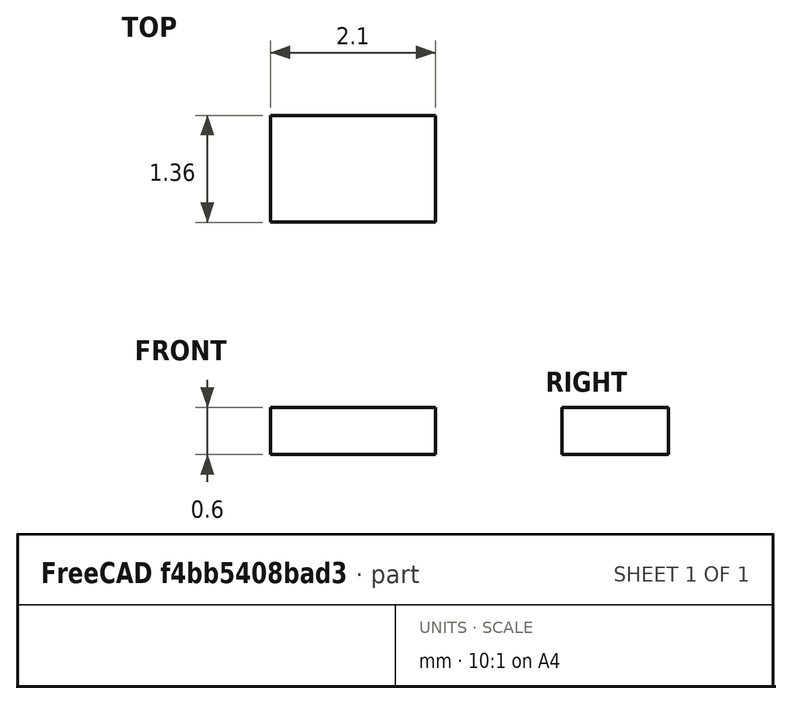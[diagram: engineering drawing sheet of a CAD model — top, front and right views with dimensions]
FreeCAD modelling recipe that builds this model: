
FCSTD DOCUMENT  (FreeCAD 0.18R15969 (Git))
Label: Resistor 10k
License: All rights reserved
LicenseURL: http://en.wikipedia.org/wiki/All_rights_reserved
objects: Sketcher::SketchObject×1, PartDesign::Pad×1, PartDesign::Body×1
note: 4 computed .brp shape members not serialized (recipe doc carries the construction recipe); baked Part::Feature solids carry a one-line shape summary decoded from their .brp

FEATURE [Sketcher::SketchObject] Sketch
  MapMode = 5
  Support = -> [XY_Plane]
  expr: Constraints[16] = 2 + 0.1
  expr: Constraints[17] = 1.25 + 0.1
  sketch-geometry (7):
    g0: LineSegment StartX=-1.05 StartY=-0.675 StartZ=0 EndX=1.05 EndY=-0.675 EndZ=0
    g1: LineSegment StartX=1.05 StartY=-0.675 StartZ=0 EndX=1.05 EndY=0.675 EndZ=0
    g2: LineSegment StartX=1.05 StartY=0.675 StartZ=0 EndX=-1.05 EndY=0.675 EndZ=0
    g3: LineSegment StartX=-1.05 StartY=0.675 StartZ=0 EndX=-1.05 EndY=-0.675 EndZ=0
    g4: LineSegment [constr] StartX=-1.05 StartY=0.675 StartZ=0 EndX=0 EndY=0 EndZ=0
    g5: LineSegment [constr] StartX=0 StartY=0 StartZ=0 EndX=1.05 EndY=0.675 EndZ=0
    g6: LineSegment [constr] StartX=0 StartY=0 StartZ=0 EndX=-1.05 EndY=-0.675 EndZ=0
  constraints (18):
    c: Coincident(g0,g1)
    c: Coincident(g1,g2)
    c: Coincident(g2,g3)
    c: Coincident(g3,g0)
    c: Horizontal(g0)
    c: Horizontal(g2)
    c: Vertical(g1)
    c: Vertical(g3)
    c: Coincident(g4,g2)
    c: Coincident(g4,g-1)
    c: Coincident(g5,g-1)
    c: Coincident(g5,g1)
    c: Coincident(g6,g-1)
    c: Coincident(g6,g0)
    c: Equal(g5,g4)
    c: Equal(g4,g6)
    c: DistanceX(g2,g2) = 2.1
    c: DistanceY(g3,g3) = 1.35
FEATURE [PartDesign::Pad] Pad
  Length = 0.6
  Length2 = 100
  Profile = -> Sketch
  Refine = true
  Type = 0
  expr: Length = 0.5 + 0.1
FEATURE [PartDesign::Body] Body  label="Resistor 10k"
  Group = -> [Sketch,Pad]
  Origin = -> Origin
  Tip = -> Pad
